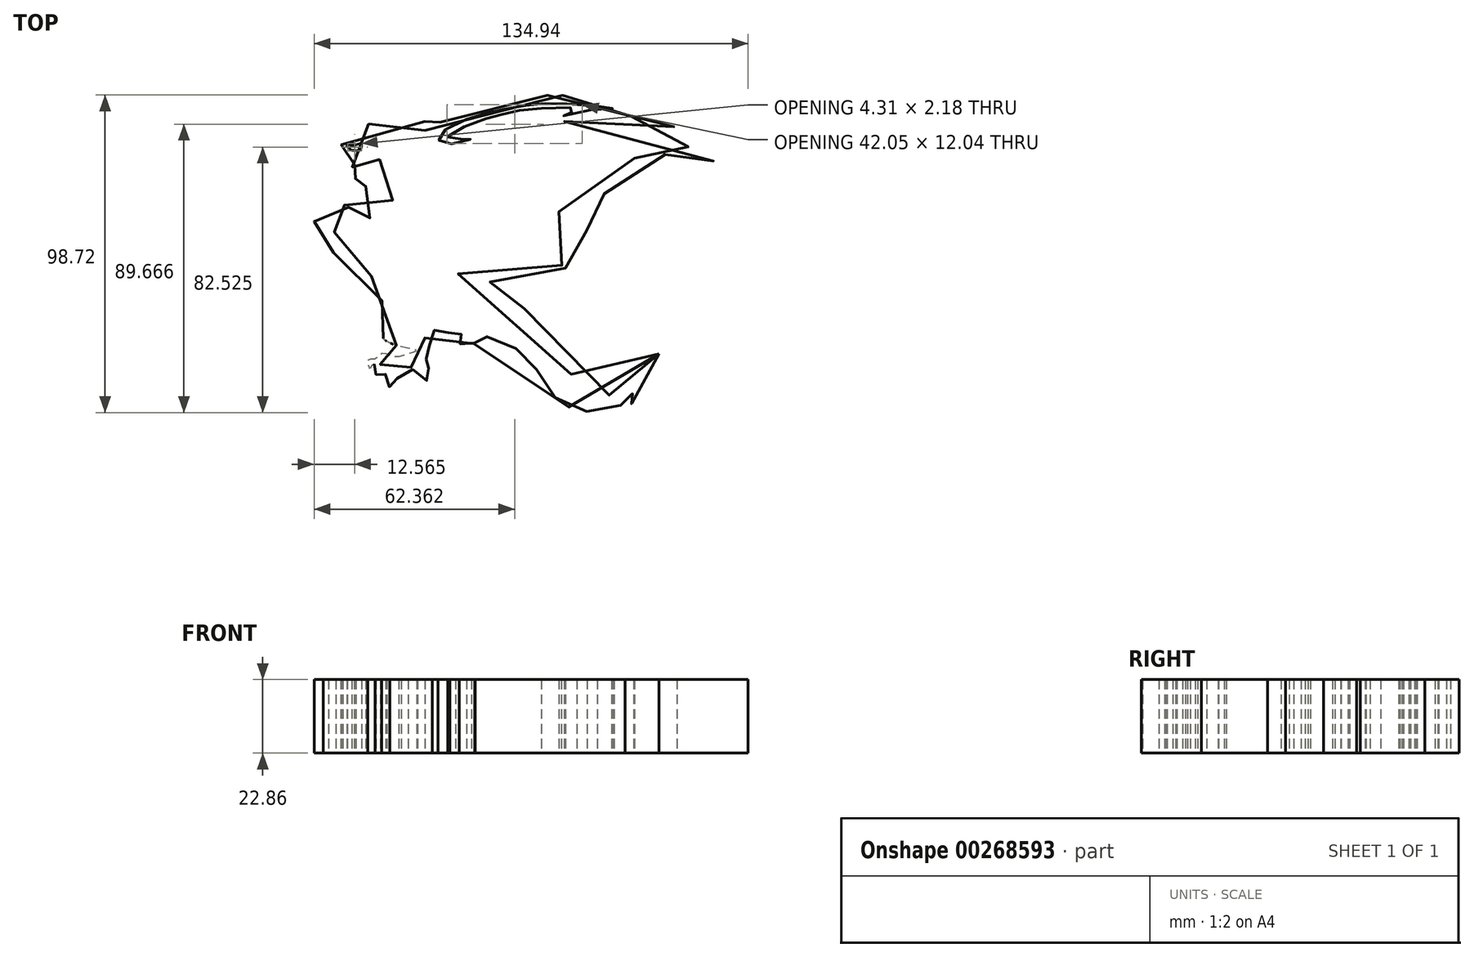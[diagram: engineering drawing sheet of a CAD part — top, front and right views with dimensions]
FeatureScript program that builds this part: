
annotation { "Feature Type Name" : "Feature", "Feature Type Description" : "" }
export const myFeature = defineFeature(function(context is Context, id is Id, definition is map)
    precondition{}
    {
        {
            var Q0;
            Q0=qCreatedBy(makeId("Top.planeOp"),FACE);
            var sketch = newSketch(context, id + "F0", { "sketchPlane" : qUnion([Q0])});
            skPoint(sketch, "E0.138.internal.snap0", {"position": v(2, 57.16) * mm});
            skFitSpline(sketch, "E0", {"points": [v(41.67, -22.95) * mm, v(31.2, -41.26) * mm, v(34.02, -34.22) * mm, v(31.6, -37.64) * mm, v(22.54, -40.86) * mm, v(12.68, -39.05) * mm, v(5.23, -31) * mm, v(1.61, -24.76) * mm, v(-5.03, -20.13) * mm, v(-12.68, -17.51) * mm, v(-15.5, -17.91) * mm, v(-15.5, -19.32) * mm, v(-18.12, -20.93) * mm, v(-20.33, -20.13) * mm, v(-18.12, -18.72) * mm, v(-19.52, -17.91) * mm, v(-20.13, -15.5) * mm, v(-23.95, -15.5) * mm, v(-23.35, -17.31) * mm, v(-26.17, -15.7) * mm, v(-30.8, -17.1) * mm, v(-30.2, -19.73) * mm, v(-27.17, -24.15) * mm, v(-33.21, -24.76) * mm, v(-30.8, -26.77) * mm, v(-28.78, -29.39) * mm, v(-30.2, -31.6) * mm, v(-31.2, -30) * mm, v(-34.22, -28.78) * mm, v(-35.63, -26.97) * mm, v(-39.05, -30.4) * mm, v(-42.87, -30.8) * mm, v(-42.07, -33.21) * mm, v(-44.48, -32.2) * mm, v(-43.28, -29.59) * mm, v(-44.48, -28.58) * mm, v(-45.09, -30.2) * mm, v(-46.5, -28.58) * mm, v(-44.89, -26.37) * mm, v(-47.5, -26.57) * mm, v(-48.1, -27.58) * mm, v(-48.71, -24.96) * mm, v(-46.3, -24.36) * mm, v(-44.48, -22.74) * mm, v(-40.46, -23.75) * mm, v(-35.22, -22.54) * mm, v(-33.61, -21.94) * mm, v(-41.67, -19.73) * mm, v(-45.7, -15.9) * mm, v(-46.1, -12.88) * mm, v(-40.86, -10.47) * mm, v(-36.23, -10.06) * mm, v(-42.67, -7.85) * mm, v(-45.9, -3.22) * mm, v(-50.52, 6.04) * mm, v(-51.13, 3.42) * mm, v(-57.16, 10.47) * mm, v(-58.77, 8.86) * mm, v(-61.8, 9.06) * mm, v(-62.6, 11.27) * mm, v(-61.4, 10.47) * mm, v(-58.77, 13.69) * mm, v(-62.2, 17.71) * mm, v(-63, 18.92) * mm, v(-65.42, 18.12) * mm, v(-64, 20.73) * mm, v(-62.4, 20.73) * mm, v(-62, 22.54) * mm, v(-57.77, 21.94) * mm, v(-56.96, 20.73) * mm, v(-56.56, 21.74) * mm, v(-57.16, 23.35) * mm, v(-54.15, 21.94) * mm, v(-54.55, 17.91) * mm, v(-54.95, 13.28) * mm, v(-52.33, 9.66) * mm, v(-49.72, 14.5) * mm, v(-48.1, 19.32) * mm, v(-43.28, 22.95) * mm, v(-39.25, 27.78) * mm, v(-42.07, 29.59) * mm, v(-46.7, 29.19) * mm, v(-49.31, 28.38) * mm, v(-47.1, 33.41) * mm, v(-41.87, 38.45) * mm, v(-43.28, 39.65) * mm, v(-45.29, 37.24) * mm, v(-51.13, 33.21) * mm, v(-52.94, 30.4) * mm, v(-52.53, 30) * mm, v(-54.75, 30) * mm, v(-57.16, 32.2) * mm, v(-54.75, 33.21) * mm, v(-49.52, 38.65) * mm, v(-53.74, 35.02) * mm, v(-58.98, 33.21) * mm, v(-60.99, 35.22) * mm, v(-59.58, 39.05) * mm, v(-58.17, 38.65) * mm, v(-55.35, 40.26) * mm, v(-56.96, 41.46) * mm, v(-55.15, 44.68) * mm, v(-49.11, 48.3) * mm, v(-40.67, 49.58) * mm, v(-34.22, 49.96) * mm, v(-31, 49.2) * mm, v(-34.22, 48.3) * mm, v(-38.45, 47.1) * mm, v(-33.65, 44.46) * mm, v(-31.57, 45.98) * mm, v(-28.22, 48.2) * mm, v(-25.7, 49.4) * mm, v(-21.33, 51.48) * mm, v(-11.07, 55.55) * mm, v(0, 57.16) * mm, v(13.89, 57.16) * mm, v(25.16, 55.15) * mm, v(35.63, 52.53) * mm, v(47.3, 46.9) * mm, v(36.83, 50.12) * mm, v(25.56, 50.9) * mm, v(12.28, 49.31) * mm, v(27.58, 48.1) * mm, v(45.7, 43.68) * mm, v(64.41, 32.6) * mm, v(69.4, 26.77) * mm, v(58.57, 34.42) * mm, v(37.64, 38.65) * mm, v(24.56, 33.01) * mm, v(22.74, 29.59) * mm, v(27.78, 25.56) * mm, v(20.53, 28.18) * mm, v(13.49, 26.77) * mm, v(10.67, 20.93) * mm, v(14.3, 16.5) * mm, v(19.32, 15.3) * mm, v(10.47, 15.3) * mm, v(5.64, 13.08) * mm, v(5.64, 8.66) * mm, v(8.86, 6.04) * mm, v(12.68, 3.62) * mm, v(8.05, 4.43) * mm, v(2, 4.46) * mm, v(-3.42, 2.62) * mm, v(-8.86, -2.01) * mm, v(-11.67, 0) * mm, v(-21.34, 1.61) * mm, v(-18.72, -1.81) * mm, v(-10.27, -3.82) * mm, v(5.43, -13.89) * mm, v(13.28, -26.17) * mm, v(14.5, -29.59) * mm, v(23.35, -35.83) * mm, v(33.82, -33.61) * mm, v(27.17, -34.02) * mm, v(34.22, -29.59) * mm, v(41.67, -22.95) * mm]});
            skFitSpline(sketch, "E1", {"points": [v(-53.74, 40.26) * mm, v(-52.94, 40.26) * mm, v(-51.33, 40.26) * mm, v(-50.92, 42.27) * mm, v(-52.94, 41.87) * mm, v(-55.35, 41.87) * mm, v(-53.74, 40.26) * mm]});
            skFitSpline(sketch, "E2", {"points": [v(-24.17, 44.46) * mm, v(-21.14, 43.7) * mm, v(-16.59, 43.9) * mm, v(-22.09, 42.37) * mm, v(-26.26, 42.94) * mm, v(-26.83, 44.65) * mm, v(-19.81, 49.2) * mm, v(-12.23, 51.67) * mm, v(-4.27, 53.56) * mm, v(4.83, 54.7) * mm, v(14.12, 54.7) * mm, v(27.4, 53.37) * mm, v(20.57, 52.8) * mm, v(11.47, 50.9) * mm, v(16.21, 53) * mm, v(6.54, 53.37) * mm, v(-3.32, 52.42) * mm, v(-9.2, 50.9) * mm, v(-15.45, 49.01) * mm, v(-24.17, 44.46) * mm]});
            skSolve(sketch);
        }
        {
            var Q0;
            Q0=makeQuery(id+"F0.imprint","IMPRINT",FACE,{"disambiguationData":[TD([[makeQuery(id+"F0.imprint","IMPRINT",EDGE,{"derivedFrom":sQuery(id+"F0.wireOp",EDGE,"E0")}),-1.0]])]});
            extrude(context, id + "F1", {"entities" : qUnion([Q0]), "depth" : 22.86 * mm, "offsetDistance" : 25.4 * mm});
        }
    });
